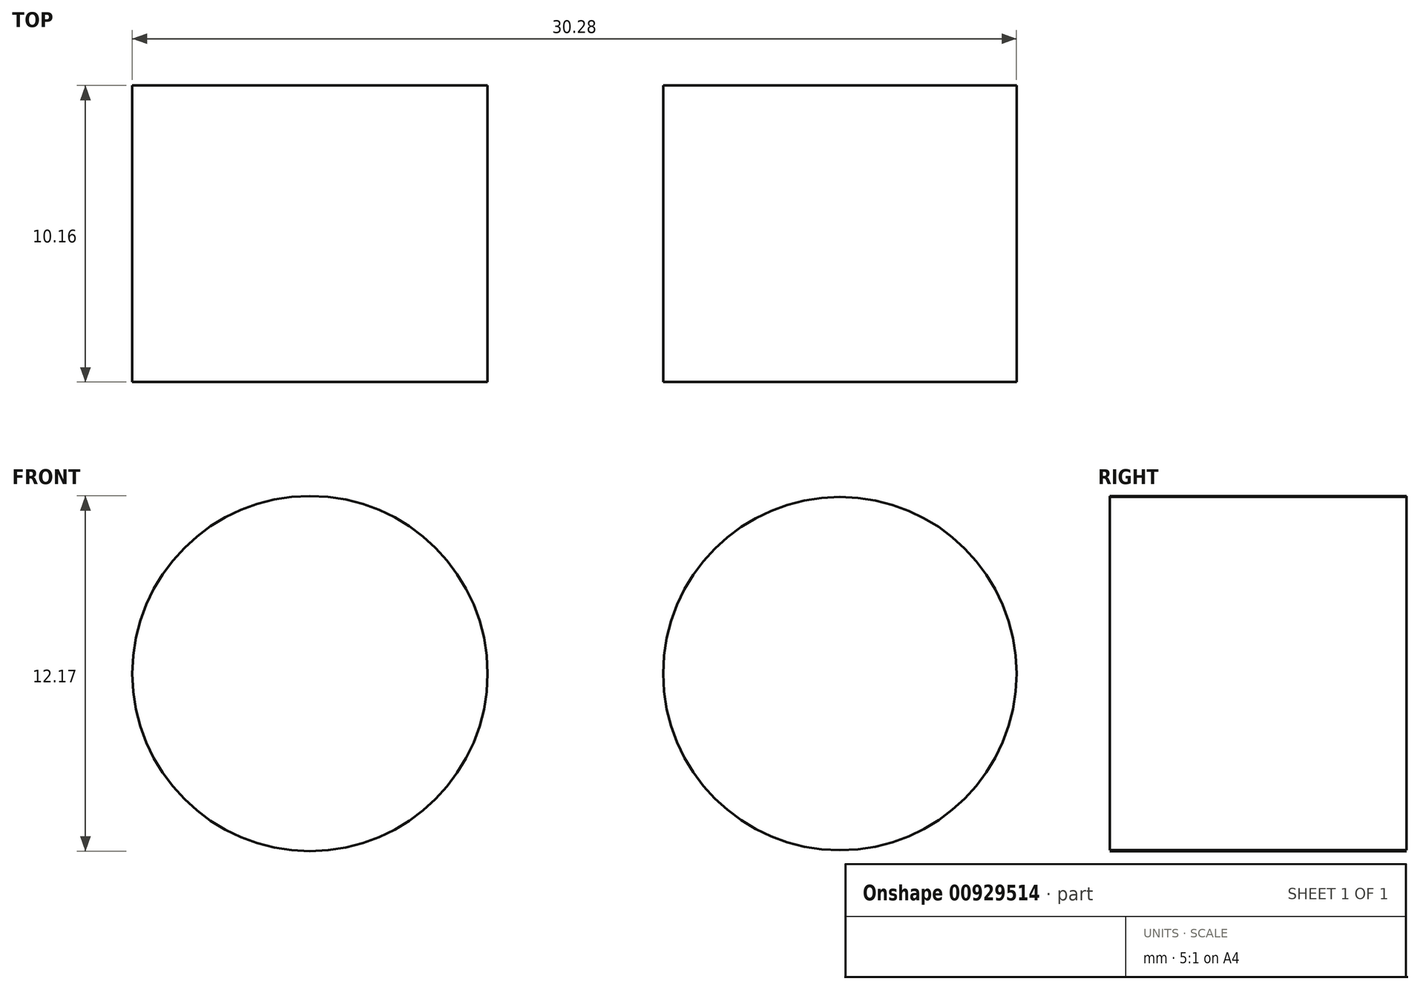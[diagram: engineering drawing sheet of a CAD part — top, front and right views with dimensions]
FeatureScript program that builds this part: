
annotation { "Feature Type Name" : "Feature", "Feature Type Description" : "" }
export const myFeature = defineFeature(function(context is Context, id is Id, definition is map)
    precondition{}
    {
        {
            var Q0;
            Q0=qCreatedBy(makeId("Front.planeOp"),FACE);
            var sketch = newSketch(context, id + "F0", { "sketchPlane" : qUnion([Q0])});
            skLineSegment(sketch, "E0.bottom", {"start": v(-61.24, 67.77) * mm, "end": v(64.13, 67.77) * mm});
            skLineSegment(sketch, "E0.top", {"start": v(-61.24, 17.62) * mm, "end": v(64.13, 17.62) * mm});
            skLineSegment(sketch, "E0.left", {"start": v(-61.24, 67.77) * mm, "end": v(-61.24, 17.62) * mm});
            skLineSegment(sketch, "E0.right", {"start": v(64.13, 67.77) * mm, "end": v(64.13, 17.62) * mm});
            skLineSegment(sketch, "E1.bottom", {"start": v(1.44, 67.77) * mm, "end": v(64.13, 67.77) * mm});
            skLineSegment(sketch, "E1.top", {"start": v(1.44, 17.62) * mm, "end": v(64.13, 17.62) * mm});
            skLineSegment(sketch, "E1.left", {"start": v(1.44, 67.77) * mm, "end": v(1.44, 17.62) * mm});
            skLineSegment(sketch, "E2.bottom", {"start": v(1.44, 67.77) * mm, "end": v(-61.24, 67.77) * mm});
            skLineSegment(sketch, "E2.top", {"start": v(1.44, 17.62) * mm, "end": v(-61.24, 17.62) * mm});
            skPoint(sketch, "E3.centerSnap0", {"position": v(-61.24, 42.7) * mm});
            skCircle(sketch, "E4", {"center": v(10.23, 42.7) * mm, "radius": 6.05 * mm});
            skPoint(sketch, "E4.centerSnap0", {"position": v(1.44, 42.7) * mm});
            skLineSegment(sketch, "E5.bottom", {"start": v(-61.53, 11.28) * mm, "end": v(64.13, 11.28) * mm});
            skLineSegment(sketch, "E5.top", {"start": v(-61.53, 17.62) * mm, "end": v(64.13, 17.62) * mm});
            skLineSegment(sketch, "E5.left", {"start": v(-61.53, 11.28) * mm, "end": v(-61.53, 17.62) * mm});
            skLineSegment(sketch, "E5.right", {"start": v(64.13, 11.28) * mm, "end": v(64.13, 17.62) * mm});
            skLineSegment(sketch, "E6", {"start": v(-63.48, 6.1) * mm, "end": v(60.72, 6.1) * mm});
            skLineSegment(sketch, "E7", {"start": v(-43.22, -6.6) * mm, "end": v(50.3, -6.6) * mm});
            skArc(sketch, "E8", {"start": v(-63.48, 6.1) * mm, "mid": v(-48.26, -41.76) * mm, "end": v(0, -55.64) * mm});
            skArc(sketch, "E9", {"start": v(0, -55.64) * mm, "mid": v(45.17, -39.35) * mm, "end": v(60.72, 6.1) * mm});
            skArc(sketch, "E10", {"start": v(-43.22, -6.6) * mm, "mid": v(-27.78, -31.1) * mm, "end": v(0, -39.35) * mm});
            skPoint(sketch, "E10.endSnap0", {"position": v(45.17, -39.35) * mm});
            skArc(sketch, "E11", {"start": v(0, -39.35) * mm, "mid": v(29.94, -30.33) * mm, "end": v(50.3, -6.6) * mm});
            skCircle(sketch, "E12", {"center": v(0, -21.29) * mm, "radius": 5.28 * mm});
            skLineSegment(sketch, "E13", {"start": v(-56.27, 11.28) * mm, "end": v(-56.27, -65.76) * mm});
            skLineSegment(sketch, "E14", {"start": v(54.83, 11.28) * mm, "end": v(54.83, -64.04) * mm});
            skLineSegment(sketch, "E15", {"start": v(-56.27, -65.76) * mm, "end": v(54.54, -65.76) * mm});
            skLineSegment(sketch, "E16", {"start": v(54.83, -64.04) * mm, "end": v(54.54, -65.76) * mm});
            skLineSegment(sketch, "E17", {"start": v(-6.19, 17.62) * mm, "end": v(-5.28, -21.15) * mm});
            skLineSegment(sketch, "E18", {"start": v(7.34, 17.62) * mm, "end": v(7.34, -21.15) * mm});
            skArc(sketch, "E19", {"start": v(7.34, -21.15) * mm, "mid": v(1.03, -14.85) * mm, "end": v(-5.28, -21.15) * mm});
            skArc(sketch, "E20", {"start": v(-5.28, -21.15) * mm, "mid": v(1.03, -28.48) * mm, "end": v(7.34, -21.15) * mm});
            skCircle(sketch, "E21", {"center": v(-7.91, 42.7) * mm, "radius": 6.08 * mm});
            skSolve(sketch);
        }
        {
            var Q0;
            Q0=makeQuery(id+"F0.imprint","IMPRINT",FACE,{"disambiguationData":[TD([[makeQuery(id+"F0.imprint","IMPRINT",EDGE,{"derivedFrom":sQuery(id+"F0.wireOp",EDGE,"E21")}),1.0]])]});
            var Q1;
            Q1=makeQuery(id+"F0.imprint","IMPRINT",FACE,{"disambiguationData":[TD([[makeQuery(id+"F0.imprint","IMPRINT",EDGE,{"derivedFrom":sQuery(id+"F0.wireOp",EDGE,"E4")}),1.0]])]});
            extrude(context, id + "F1", {"entities" : qUnion([Q0, Q1]), "depth" : 10.16 * mm, "offsetDistance" : 25.4 * mm});
        }
    });
